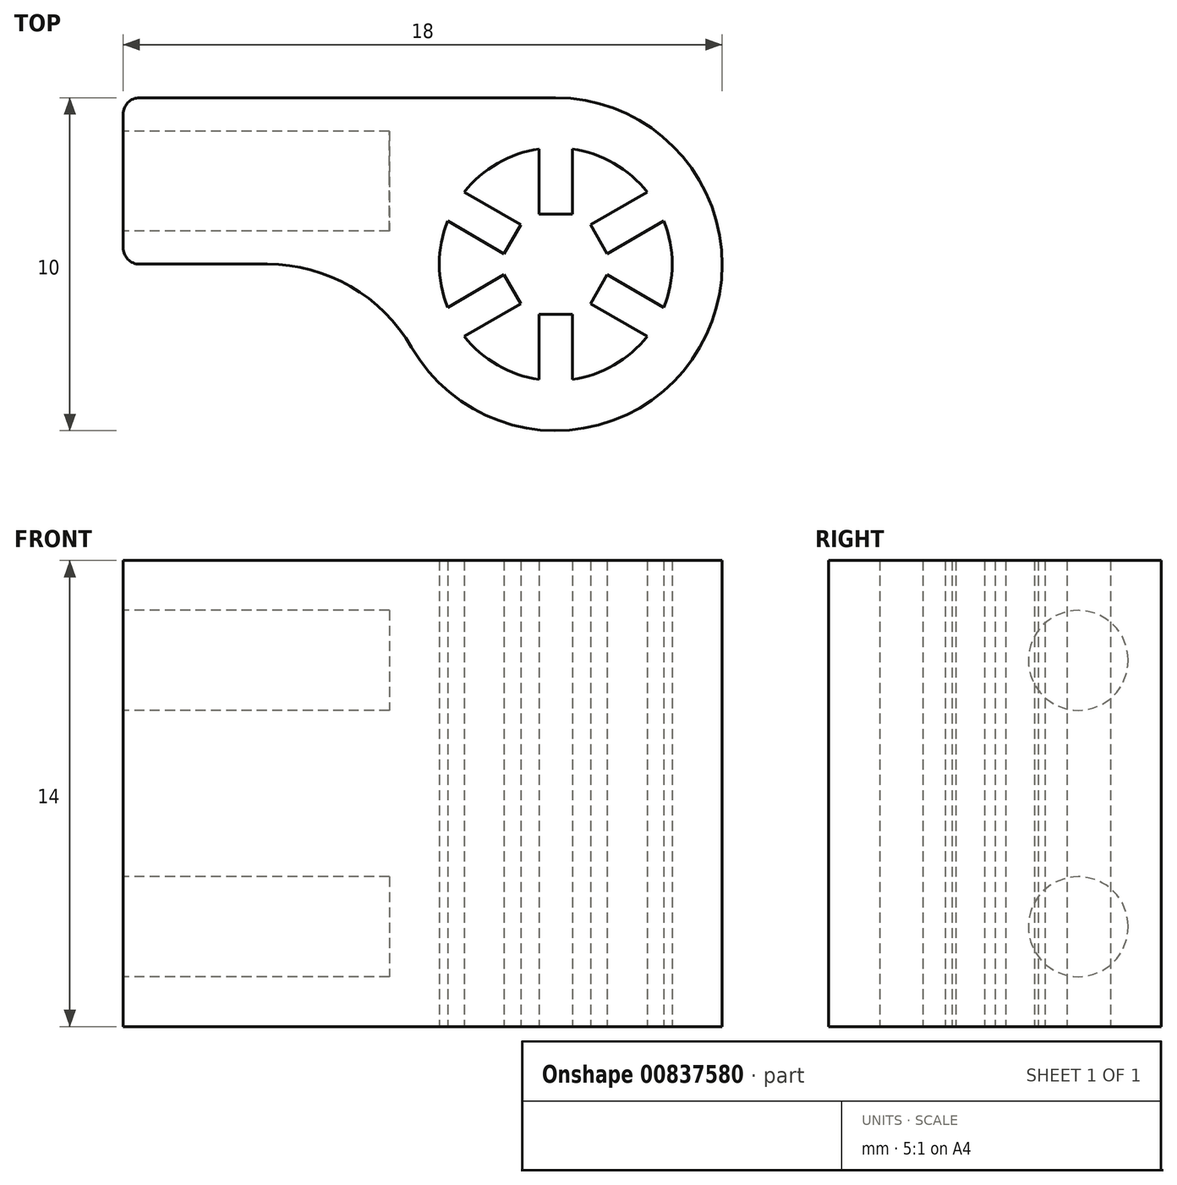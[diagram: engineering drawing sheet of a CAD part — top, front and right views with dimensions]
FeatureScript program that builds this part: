
annotation { "Feature Type Name" : "Feature", "Feature Type Description" : "" }
export const myFeature = defineFeature(function(context is Context, id is Id, definition is map)
    precondition{}
    {
        {
            var Q0;
            Q0=qCreatedBy(makeId("Top.planeOp"),FACE);
            var sketch = newSketch(context, id + "F0", { "sketchPlane" : qUnion([Q0])});
            skCircle(sketch, "E0", {"center": v(0, 0) * mm, "radius": 1.5 * mm, "construction": true});
            skArc(sketch, "E1", {"start": v(-0.5, 3.46) * mm, "mid": v(-1.75, 3.03) * mm, "end": v(-2.75, 2.17) * mm});
            skLineSegment(sketch, "E2.top", {"start": v(-0.5, 1.5) * mm, "end": v(0.5, 1.5) * mm});
            skLineSegment(sketch, "E2.left", {"start": v(-0.5, 3.46) * mm, "end": v(-0.5, 1.5) * mm});
            skLineSegment(sketch, "E2.right", {"start": v(0.5, 3.46) * mm, "end": v(0.5, 1.5) * mm});
            skCircle(sketch, "E3", {"center": v(0, 0) * mm, "radius": 5 * mm});
            skLineSegment(sketch, "E4", {"start": v(0, 0) * mm, "end": v(0, 4.33) * mm, "construction": true});
            skLineSegment(sketch, "E5.1.0", {"start": v(-3.25, 1.3) * mm, "end": v(-1.55, 0.32) * mm});
            skLineSegment(sketch, "E5.1.1", {"start": v(-1.55, 0.32) * mm, "end": v(-1.05, 1.18) * mm});
            skLineSegment(sketch, "E5.1.2", {"start": v(-2.75, 2.17) * mm, "end": v(-1.05, 1.18) * mm});
            skLineSegment(sketch, "E5.2.0", {"start": v(-2.75, -2.17) * mm, "end": v(-1.05, -1.18) * mm});
            skLineSegment(sketch, "E5.2.1", {"start": v(-1.05, -1.18) * mm, "end": v(-1.55, -0.32) * mm});
            skLineSegment(sketch, "E5.2.2", {"start": v(-3.25, -1.3) * mm, "end": v(-1.55, -0.32) * mm});
            skLineSegment(sketch, "E6.2.3.0", {"start": v(0.5, -3.46) * mm, "end": v(0.5, -1.5) * mm});
            skLineSegment(sketch, "E6.3.3.0", {"start": v(0.5, -1.5) * mm, "end": v(-0.5, -1.5) * mm});
            skLineSegment(sketch, "E6.6.3.0", {"start": v(-0.5, -3.46) * mm, "end": v(-0.5, -1.5) * mm});
            skLineSegment(sketch, "E6.2.4.0", {"start": v(3.25, -1.3) * mm, "end": v(1.55, -0.32) * mm});
            skLineSegment(sketch, "E6.3.4.0", {"start": v(1.55, -0.32) * mm, "end": v(1.05, -1.18) * mm});
            skLineSegment(sketch, "E6.6.4.0", {"start": v(2.75, -2.17) * mm, "end": v(1.05, -1.18) * mm});
            skLineSegment(sketch, "E6.2.5.0", {"start": v(2.75, 2.17) * mm, "end": v(1.05, 1.18) * mm});
            skLineSegment(sketch, "E6.3.5.0", {"start": v(1.05, 1.18) * mm, "end": v(1.55, 0.32) * mm});
            skLineSegment(sketch, "E6.6.5.0", {"start": v(3.25, 1.3) * mm, "end": v(1.55, 0.32) * mm});
            skArc(sketch, "E7.trimOffspring", {"start": v(-3.25, 1.3) * mm, "mid": v(-3.5, 0) * mm, "end": v(-3.25, -1.3) * mm});
            skArc(sketch, "E8.trimOffspring", {"start": v(-2.75, -2.17) * mm, "mid": v(-1.75, -3.03) * mm, "end": v(-0.5, -3.46) * mm});
            skArc(sketch, "E9.trimOffspring", {"start": v(0.5, -3.46) * mm, "mid": v(1.75, -3.03) * mm, "end": v(2.75, -2.17) * mm});
            skArc(sketch, "E10.trimOffspring", {"start": v(3.25, -1.3) * mm, "mid": v(3.5, 0) * mm, "end": v(3.25, 1.3) * mm});
            skArc(sketch, "E11.trimOffspring", {"start": v(2.75, 2.17) * mm, "mid": v(-3.03, -1.75) * mm, "end": v(3.25, 1.3) * mm});
            skArc(sketch, "E12.trimOffspring", {"start": v(2.75, 2.17) * mm, "mid": v(1.75, 3.03) * mm, "end": v(0.5, 3.46) * mm});
            skLineSegment(sketch, "E13", {"start": v(0, 5) * mm, "end": v(-13, 5) * mm});
            skLineSegment(sketch, "E14", {"start": v(-13, 5) * mm, "end": v(-13, 0) * mm});
            skLineSegment(sketch, "E15", {"start": v(-13, 0) * mm, "end": v(-5, 0) * mm});
            skSolve(sketch);
        }
        {
            var Q0;
            Q0=makeQuery(id+"F0.imprint","IMPRINT",FACE,{"disambiguationData":[TD([[makeQuery(id+"F0.imprint","IMPRINT",EDGE,{"derivedFrom":sQuery(id+"F0.wireOp",EDGE,"E3")}),1.0]])]});
            var Q1;
            {var subQ0=sQuery(id+"F0.wireOp",EDGE,"E5.1.0");Q1=makeQuery(id+"F0.imprint","IMPRINT",FACE,{"disambiguationData":[TD([[makeQuery(id+"F0.imprint","IMPRINT",EDGE,{"derivedFrom":subQ0}),1.0]])]});}
            var Q2;
            Q2=makeQuery(id+"F0.imprint","IMPRINT",FACE,{"disambiguationData":[TD([[makeQuery(id+"F0.imprint","IMPRINT",EDGE,{"derivedFrom":sQuery(id+"F0.wireOp",EDGE,"E2.top")}),1.0]])]});
            var Q3;
            {var subQ0=sQuery(id+"F0.wireOp",EDGE,"E5.2.0");Q3=makeQuery(id+"F0.imprint","IMPRINT",FACE,{"disambiguationData":[TD([[makeQuery(id+"F0.imprint","IMPRINT",EDGE,{"derivedFrom":subQ0}),1.0]])]});}
            var Q4;
            {var subQ0=sQuery(id+"F0.wireOp",EDGE,"E6.2.3.0");Q4=makeQuery(id+"F0.imprint","IMPRINT",FACE,{"disambiguationData":[TD([[makeQuery(id+"F0.imprint","IMPRINT",EDGE,{"derivedFrom":subQ0}),1.0]])]});}
            var Q5;
            {var subQ0=sQuery(id+"F0.wireOp",EDGE,"E6.2.4.0");Q5=makeQuery(id+"F0.imprint","IMPRINT",FACE,{"disambiguationData":[TD([[makeQuery(id+"F0.imprint","IMPRINT",EDGE,{"derivedFrom":subQ0}),1.0]])]});}
            var Q6;
            {var subQ0=sQuery(id+"F0.wireOp",EDGE,"E13");Q6=makeQuery(id+"F0.imprint","IMPRINT",FACE,{"disambiguationData":[TD([[makeQuery(id+"F0.imprint","IMPRINT",EDGE,{"derivedFrom":subQ0}),1.0]])]});}
            extrude(context, id + "F1", {"entities" : qUnion([Q0, Q1, Q2, Q3, Q4, Q5, Q6]), "endBound" : BoundingType.SYMMETRIC, "depth" : 14 * mm, "offsetDistance" : 25 * mm});
        }
        {
            var Q0;
            Q0=makeQuery(id+"F1.opExtrude","SWEPT_EDGE",EDGE,{"disambiguationData":[OSD([sQuery(id+"F0.wireOp",EDGE,"E3"),sQuery(id+"F0.wireOp",EDGE,"E15")])]});
            fillet(context, id + "F2", {"entities" : qUnion([Q0]), "radius" : 5 * mm, "tangentPropagation" : true, "allowEdgeOverflow" : false});
        }
        {
            var Q0;
            Q0=makeQuery(id+"F1.opExtrude","SWEPT_EDGE",EDGE,{"disambiguationData":[OSD([sQuery(id+"F0.wireOp",EDGE,"E13"),sQuery(id+"F0.wireOp",EDGE,"E14")])]});
            var Q1;
            Q1=makeQuery(id+"F1.opExtrude","SWEPT_EDGE",EDGE,{"disambiguationData":[OSD([sQuery(id+"F0.wireOp",EDGE,"E14"),sQuery(id+"F0.wireOp",EDGE,"E15")])]});
            fillet(context, id + "F3", {"entities" : qUnion([Q0, Q1]), "radius" : 0.5 * mm, "tangentPropagation" : true, "allowEdgeOverflow" : false});
        }
        {
            var Q0;
            Q0=makeQuery(id+"F1.opExtrude","SWEPT_FACE",FACE,{"disambiguationData":[OSD([sQuery(id+"F0.wireOp",EDGE,"E14")])]});
            var sketch = newSketch(context, id + "F4", { "sketchPlane" : qUnion([Q0])});
            skCircle(sketch, "E16", {"center": v(-2.5, -4) * mm, "radius": 1.5 * mm});
            skCircle(sketch, "E17", {"center": v(-2.5, 4) * mm, "radius": 1.5 * mm});
            skLineSegment(sketch, "E18", {"start": v(-14.35, 0) * mm, "end": v(11.95, 0) * mm, "construction": true});
            skSolve(sketch);
        }
        {
            var Q0;
            Q0=makeQuery(id+"F4.imprint","IMPRINT",FACE,{"disambiguationData":[TD([[makeQuery(id+"F4.imprint","IMPRINT",EDGE,{"derivedFrom":sQuery(id+"F4.wireOp",EDGE,"E17")}),1.0]])]});
            var Q1;
            Q1=makeQuery(id+"F4.imprint","IMPRINT",FACE,{"disambiguationData":[TD([[makeQuery(id+"F4.imprint","IMPRINT",EDGE,{"derivedFrom":sQuery(id+"F4.wireOp",EDGE,"E16")}),1.0]])]});
            extrude(context, id + "F5", {"entities" : qUnion([Q0, Q1]), "operationType" : NewBodyOperationType.REMOVE, "oppositeDirection" : true, "depth" : 8 * mm, "offsetDistance" : 25 * mm});
        }
    });
